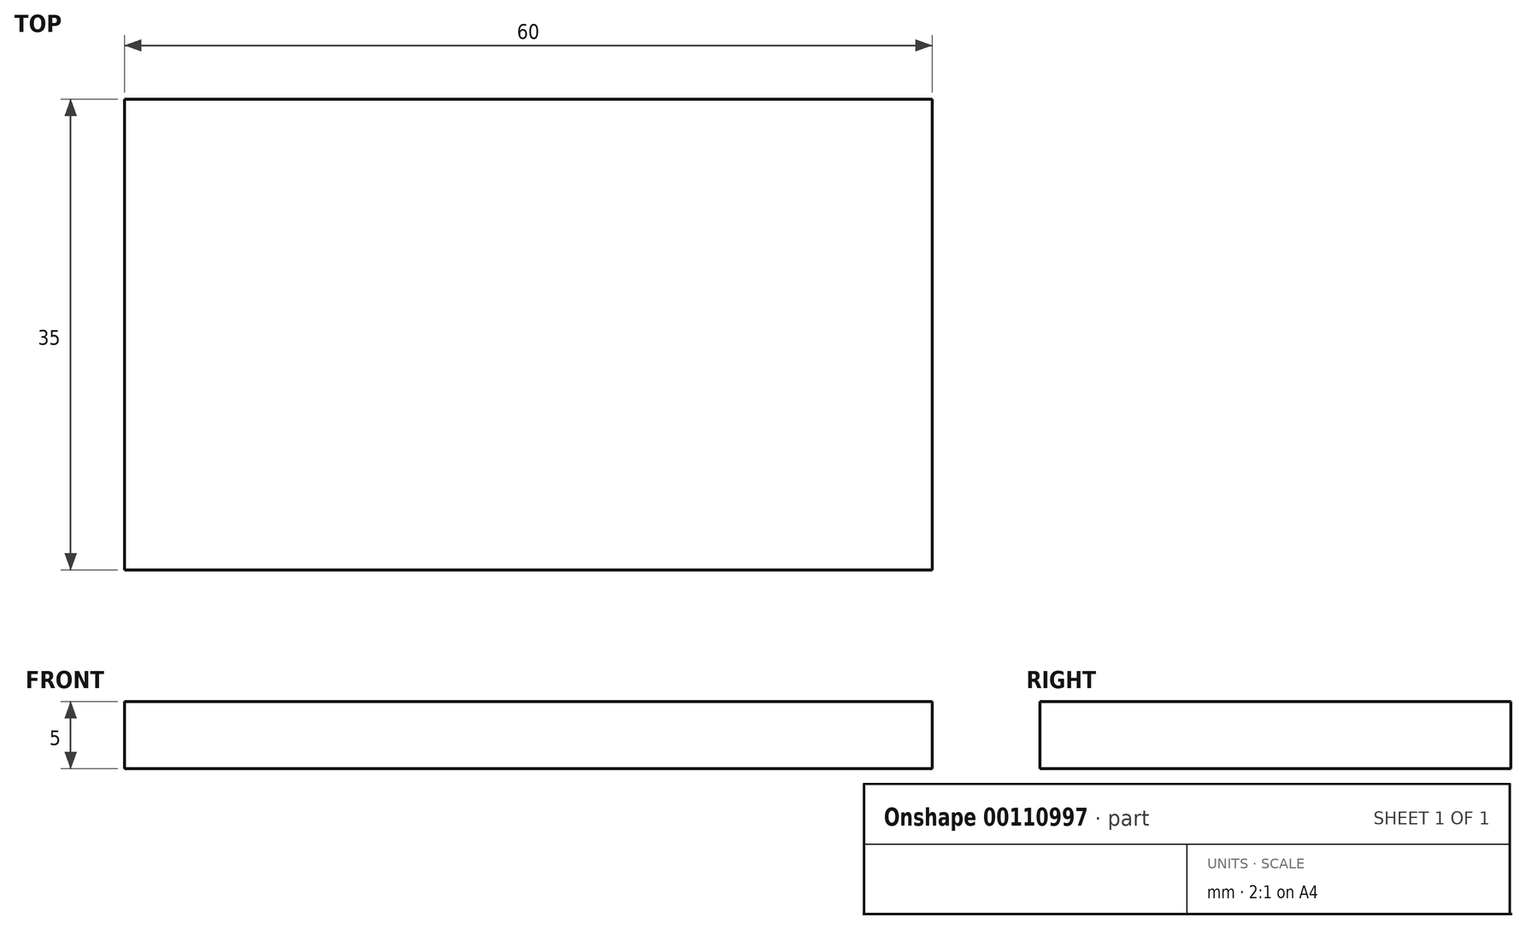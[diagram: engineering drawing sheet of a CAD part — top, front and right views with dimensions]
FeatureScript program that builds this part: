
annotation { "Feature Type Name" : "Feature", "Feature Type Description" : "" }
export const myFeature = defineFeature(function(context is Context, id is Id, definition is map)
    precondition{}
    {
        {
            var Q0;
            Q0=qCreatedBy(makeId("Top.planeOp"),FACE);
            var sketch = newSketch(context, id + "F0", { "sketchPlane" : qUnion([Q0])});
            skLineSegment(sketch, "E0.bottom", {"start": v(30, 17.5) * mm, "end": v(-30, 17.5) * mm});
            skLineSegment(sketch, "E0.top", {"start": v(30, -17.5) * mm, "end": v(-30, -17.5) * mm});
            skLineSegment(sketch, "E0.left", {"start": v(30, 17.5) * mm, "end": v(30, -17.5) * mm});
            skLineSegment(sketch, "E0.right", {"start": v(-30, 17.5) * mm, "end": v(-30, -17.5) * mm});
            skPoint(sketch, "E0.middle", {"position": v(0, 0) * mm});
            skSolve(sketch);
        }
        {
            var Q0;
            Q0=makeQuery(id+"F0.imprint","IMPRINT",FACE,{"disambiguationData":[TD([[makeQuery(id+"F0.imprint","IMPRINT",EDGE,{"derivedFrom":sQuery(id+"F0.wireOp",EDGE,"E0.bottom")}),1.0]])]});
            extrude(context, id + "F1", {"entities" : qUnion([Q0]), "depth" : 5 * mm});
        }
    });
